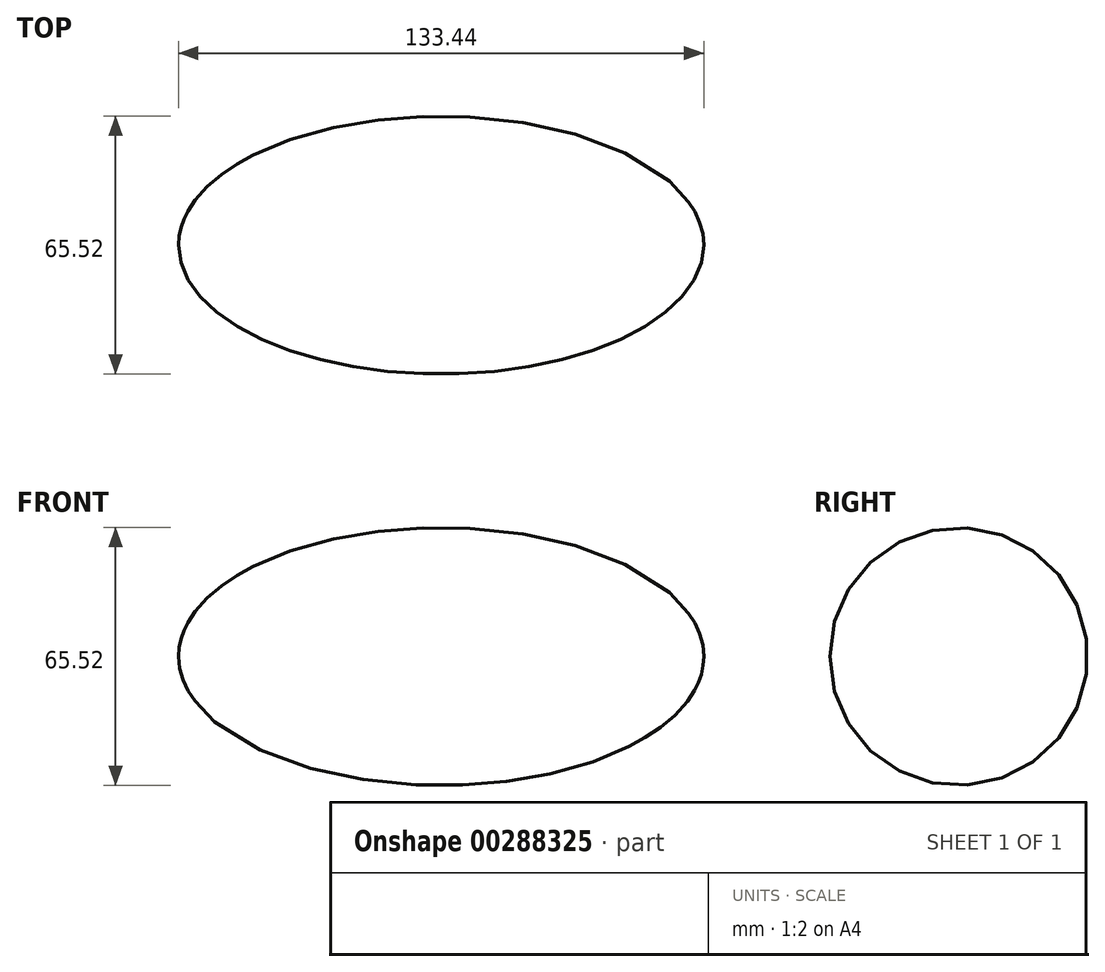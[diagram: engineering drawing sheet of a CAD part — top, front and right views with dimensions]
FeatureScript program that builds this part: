
annotation { "Feature Type Name" : "Feature", "Feature Type Description" : "" }
export const myFeature = defineFeature(function(context is Context, id is Id, definition is map)
    precondition{}
    {
        {
            var Q0;
            Q0=qCreatedBy(makeId("Top.planeOp"),FACE);
            var sketch = newSketch(context, id + "F0", { "sketchPlane" : qUnion([Q0])});
            skEllipticalArc(sketch, "E0", {});
            skLineSegment(sketch, "E1", {"start": v(-66.72, 0) * mm, "end": v(66.72, 0) * mm});
            const initialGuessF0  = {"E0": [0, 0, -1, 0, 0.06671974807977676, 0.03275583609283888, 0, 3.141592653589793]};
            skSetInitialGuess(sketch, initialGuessF0);
            skSolve(sketch);
        }
        {
            var Q0;
            Q0=makeQuery(id+"F0.imprint","IMPRINT",FACE,{"disambiguationData":[TD([[makeQuery(id+"F0.imprint","IMPRINT",EDGE,{"derivedFrom":sQuery(id+"F0.wireOp",EDGE,"E0")}),1.0]])]});
            var Q1;
            Q1=sQuery(id+"F0.wireOp",EDGE,"E1");
            revolve(context, id + "F1", {"entities" : qUnion([Q0]), "axis" : qUnion([Q1]), "revolveType" : RevolveType.FULL});
        }
    });
